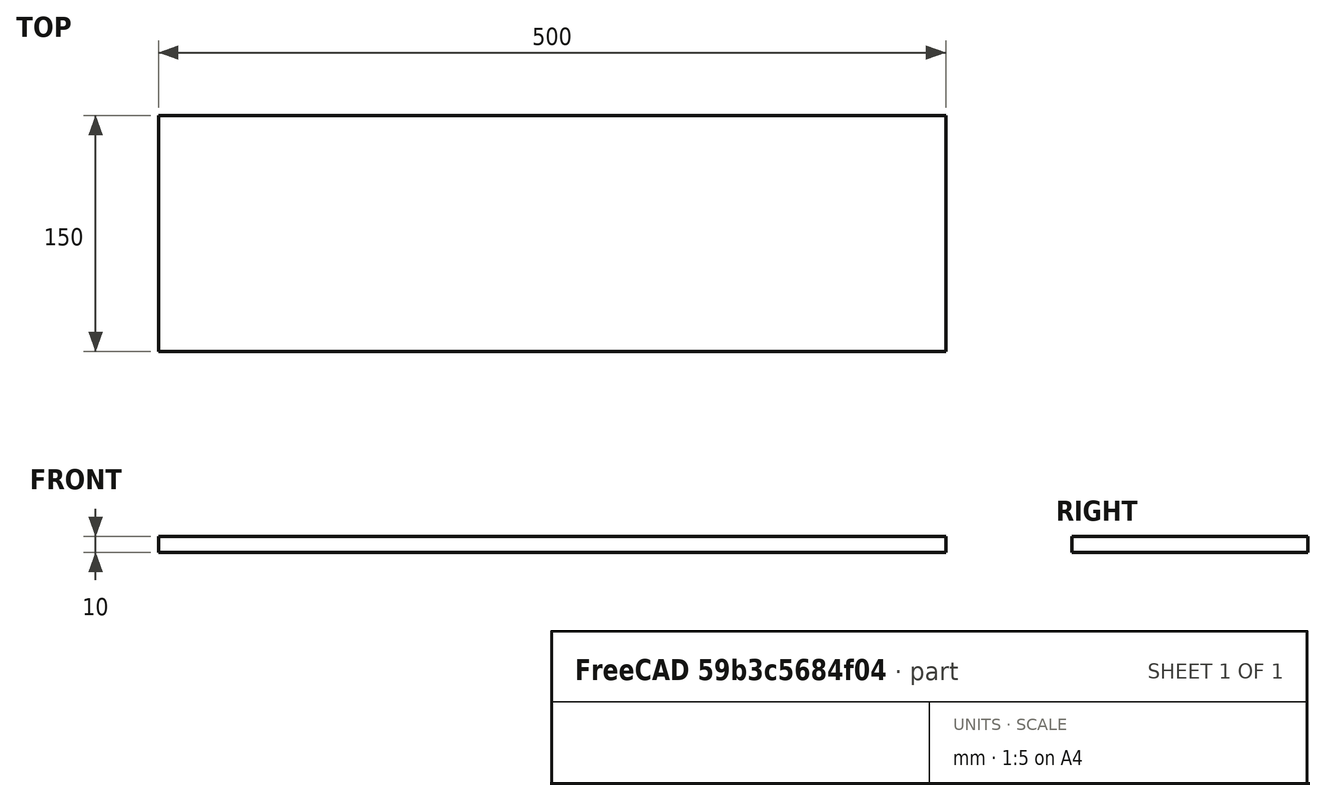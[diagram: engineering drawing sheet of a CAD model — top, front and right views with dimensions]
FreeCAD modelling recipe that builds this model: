
FCSTD DOCUMENT  (FreeCAD 0.19R14555 (Git shallow))
Label: Name
License: All rights reserved
LicenseURL: http://en.wikipedia.org/wiki/All_rights_reserved
objects: Part::Extrusion×5, Part::Part2DObjectPython×1, App::FeaturePython×1
note: 6 computed .brp shape members not serialized (recipe doc carries the construction recipe); baked Part::Feature solids carry a one-line shape summary decoded from their .brp

FEATURE [Part::Part2DObjectPython] Rectangle  # Draft 2D object (typed FeaturePython)
  Area = 0
  ChamferSize = 0
  Columns = 1
  FilletRadius = 0
  Height = 150
  Length = 500
  MakeFace = false
  Placement = pos=(-49.9799,-49.9119,0) rot=(0,0,1;0rad)
  Rows = 1
FEATURE [App::FeaturePython] Text  # WARN: FeaturePython — macro-defined, semantics opaque (R4)
  Placement = pos=(-30,0,0) rot=(0,0,1;0rad)
  Text = Mens Shed
FEATURE [Part::Extrusion] Extrude
  Base = -> Rectangle
  Dir = (0,0,1)
  DirMode = 2
  FaceMakerClass = Part::FaceMakerBullseye
  LengthFwd = 10
  LengthRev = 0
  Solid = false
  Symmetric = false
FEATURE [Part::Extrusion] Extrude001
  Base = -> Rectangle
  Dir = (0,0,1)
  DirMode = 2
  FaceMakerClass = Part::FaceMakerBullseye
  LengthFwd = 10
  LengthRev = 0
  Solid = true
  Symmetric = false
FEATURE [Part::Extrusion] Extrude002
  Base = -> Rectangle
  Dir = (0,0,1)
  DirMode = 2
  FaceMakerClass = Part::FaceMakerBullseye
  LengthFwd = 10
  LengthRev = 0
  Solid = false
  Symmetric = false
FEATURE [Part::Extrusion] Extrude003
  Base = -> Rectangle
  Dir = (0,0,1)
  DirMode = 2
  FaceMakerClass = Part::FaceMakerBullseye
  LengthFwd = 10
  LengthRev = 0
  Solid = false
  Symmetric = false
FEATURE [Part::Extrusion] Extrude004
  Base = -> Rectangle
  Dir = (0,0,1)
  DirMode = 2
  FaceMakerClass = Part::FaceMakerBullseye
  LengthFwd = 10
  LengthRev = 0
  Solid = false
  Symmetric = false
